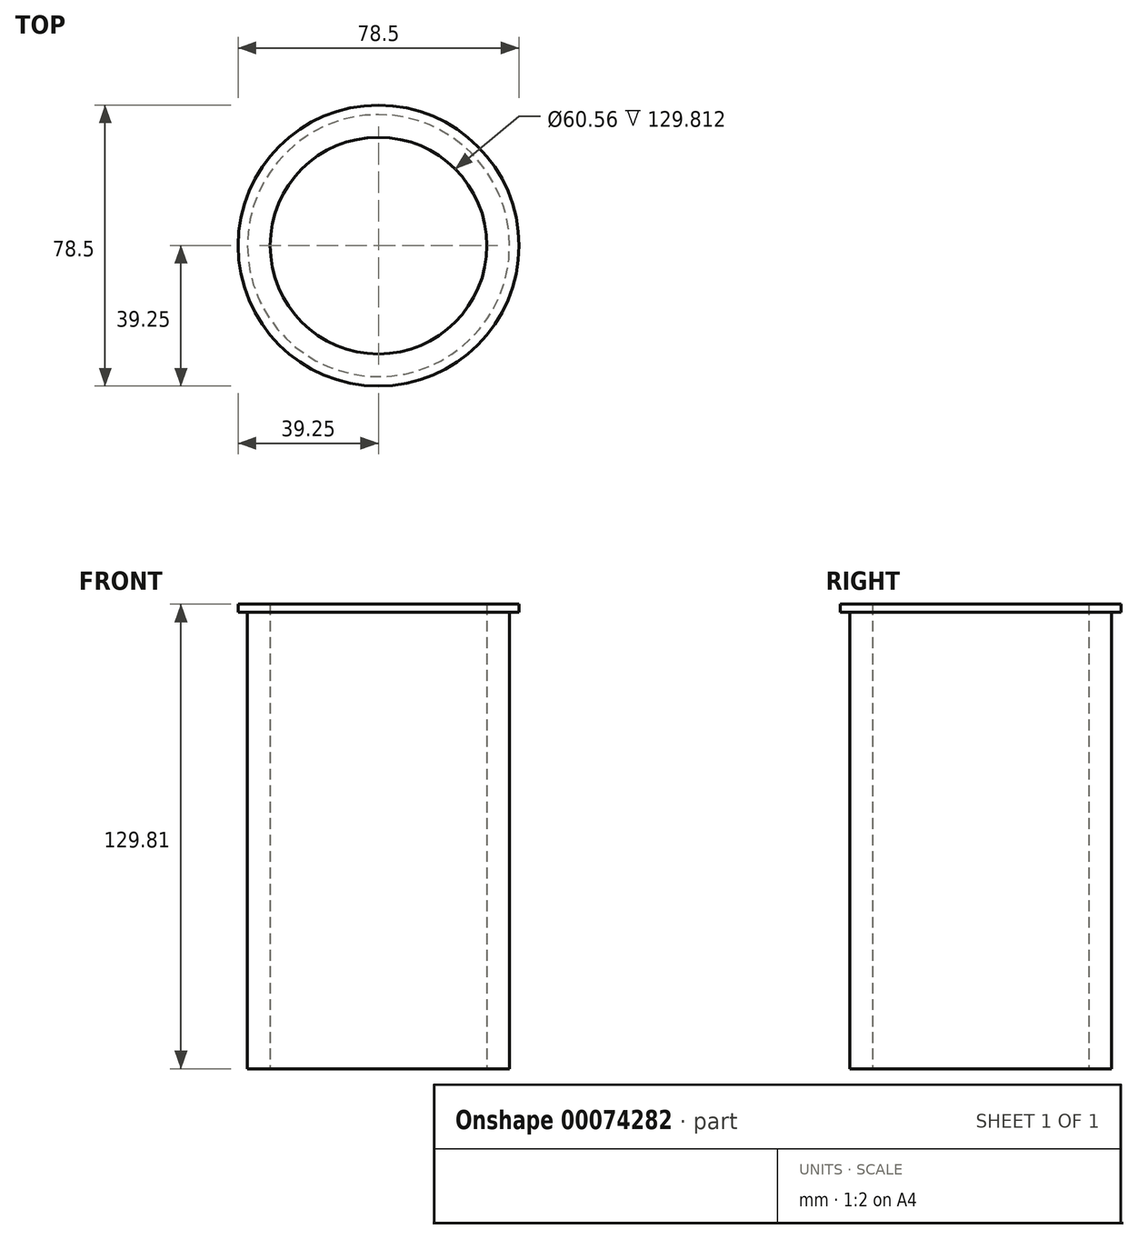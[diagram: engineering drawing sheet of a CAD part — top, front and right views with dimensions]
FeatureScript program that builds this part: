
annotation { "Feature Type Name" : "Feature", "Feature Type Description" : "" }
export const myFeature = defineFeature(function(context is Context, id is Id, definition is map)
    precondition{}
    {
        {
            var Q0;
            Q0=qCreatedBy(makeId("Top.planeOp"),FACE);
            var sketch = newSketch(context, id + "F0", { "sketchPlane" : qUnion([Q0])});
            skCircle(sketch, "E0", {"center": v(0, 0) * mm, "radius": 39.25 * mm});
            skCircle(sketch, "E1", {"center": v(0, 0) * mm, "radius": 30.28 * mm});
            skSolve(sketch);
        }
        {
            var Q0;
            Q0=makeQuery(id+"F0.imprint","IMPRINT",FACE,{"disambiguationData":[TD([[makeQuery(id+"F0.imprint","IMPRINT",EDGE,{"derivedFrom":sQuery(id+"F0.wireOp",EDGE,"E0")}),1.0]])]});
            extrude(context, id + "F1", {"entities" : qUnion([Q0]), "depth" : 60.2 * mm, "hasSecondDirection" : true, "secondDirectionOppositeDirection" : true, "secondDirectionDepth" : 69.61 * mm});
        }
        {
            var Q0;
            Q0=makeQuery(id+"F1.opExtrude","CAP_FACE",FACE,{"disambiguationData":[OSD([sQuery(id+"F0.wireOp",EDGE,"E0"),sQuery(id+"F0.wireOp",EDGE,"E1")])],"isStart":true});
            var sketch = newSketch(context, id + "F2", { "sketchPlane" : qUnion([Q0])});
            skCircle(sketch, "E2", {"center": v(0, 0) * mm, "radius": 36.62 * mm});
            skSolve(sketch);
        }
        {
            var Q0;
            Q0=makeQuery(id+"F2.imprint","IMPRINT",FACE,{"disambiguationData":[TD([[makeQuery(id+"F2.imprint","IMPRINT",EDGE,{"derivedFrom":sQuery(id+"F2.wireOp",EDGE,"E2")}),-1.0]])]});
            extrude(context, id + "F3", {"entities" : qUnion([Q0]), "operationType" : NewBodyOperationType.REMOVE, "oppositeDirection" : true, "depth" : 127.54 * mm, "hasSecondDirection" : true, "secondDirectionOppositeDirection" : false, "secondDirectionDepth" : 1.65 * mm});
        }
    });
